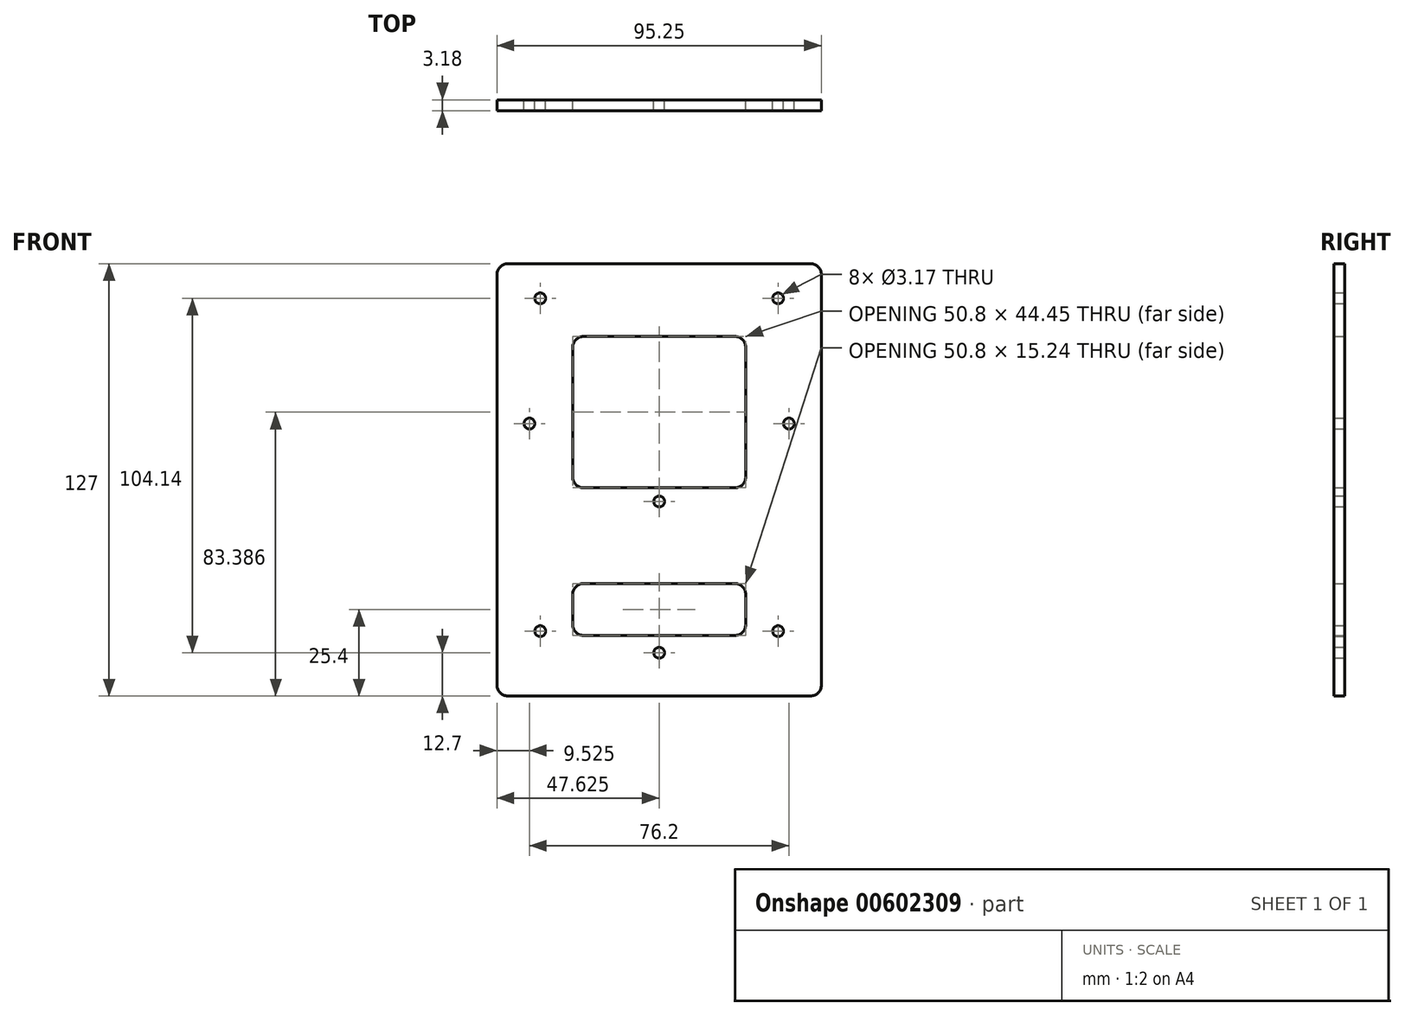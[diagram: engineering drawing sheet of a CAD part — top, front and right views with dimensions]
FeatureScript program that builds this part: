
annotation { "Feature Type Name" : "Feature", "Feature Type Description" : "" }
export const myFeature = defineFeature(function(context is Context, id is Id, definition is map)
    precondition{}
    {
        {
            var Q0;
            Q0=qCreatedBy(makeId("Front.planeOp"),FACE);
            var sketch = newSketch(context, id + "F0", { "sketchPlane" : qUnion([Q0])});
            skLineSegment(sketch, "E0.bottom", {"start": v(3.17, 0) * mm, "end": v(92.08, 0) * mm});
            skLineSegment(sketch, "E1.MirrorCS", {"start": v(0, -3.17) * mm, "end": v(0, -123.83) * mm});
            skLineSegment(sketch, "E2.MirrorCS", {"start": v(95.25, -3.17) * mm, "end": v(95.25, -123.83) * mm});
            skCircle(sketch, "E3.MirrorC", {"center": v(85.73, -46.95) * mm, "radius": 31.75 * mm, "construction": true});
            skCircle(sketch, "E4.MirrorC", {"center": v(47.63, -69.85) * mm, "radius": 31.75 * mm, "construction": true});
            skCircle(sketch, "E5.MirrorC", {"center": v(85.73, -46.95) * mm, "radius": 1.59 * mm});
            skLineSegment(sketch, "E6.MirrorCS", {"start": v(47.63, -127) * mm, "end": v(47.62, 0) * mm, "construction": true});
            skLineSegment(sketch, "E7.MirrorCS", {"start": v(3.17, -127) * mm, "end": v(92.08, -127) * mm});
            skCircle(sketch, "E8.MirrorC", {"center": v(9.52, -46.95) * mm, "radius": 1.59 * mm});
            skCircle(sketch, "E9.MirrorC", {"center": v(9.52, -46.95) * mm, "radius": 31.75 * mm, "construction": true});
            skCircle(sketch, "E10.MirrorC", {"center": v(47.63, -69.85) * mm, "radius": 1.59 * mm});
            skCircle(sketch, "E11.MirrorC", {"center": v(47.63, -69.85) * mm, "radius": 12.7 * mm, "construction": true});
            skCircle(sketch, "E12.MirrorC", {"center": v(47.62, -114.3) * mm, "radius": 12.7 * mm, "construction": true});
            skCircle(sketch, "E13.MirrorC", {"center": v(47.62, -114.3) * mm, "radius": 1.59 * mm});
            skCircle(sketch, "E14", {"center": v(12.7, -10.16) * mm, "radius": 1.59 * mm});
            skCircle(sketch, "E15", {"center": v(12.7, -107.95) * mm, "radius": 1.59 * mm});
            skCircle(sketch, "E16.MirrorC", {"center": v(82.55, -10.16) * mm, "radius": 1.59 * mm});
            skCircle(sketch, "E17.MirrorC", {"center": v(82.55, -107.95) * mm, "radius": 1.59 * mm});
            skLineSegment(sketch, "E18.bottom", {"start": v(25.4, -21.39) * mm, "end": v(69.85, -21.39) * mm});
            skLineSegment(sketch, "E18.top", {"start": v(25.4, -65.84) * mm, "end": v(69.85, -65.84) * mm});
            skLineSegment(sketch, "E18.left", {"start": v(22.23, -24.56) * mm, "end": v(22.23, -62.66) * mm});
            skLineSegment(sketch, "E18.right", {"start": v(73.03, -24.56) * mm, "end": v(73.03, -62.66) * mm});
            skPoint(sketch, "E18.middle", {"position": v(47.63, -43.61) * mm});
            skLineSegment(sketch, "E19.bottom", {"start": v(69.85, -93.98) * mm, "end": v(25.4, -93.98) * mm});
            skLineSegment(sketch, "E19.top", {"start": v(69.85, -109.22) * mm, "end": v(25.4, -109.22) * mm});
            skLineSegment(sketch, "E19.left", {"start": v(73.03, -97.15) * mm, "end": v(73.03, -106.05) * mm});
            skLineSegment(sketch, "E19.right", {"start": v(22.23, -97.15) * mm, "end": v(22.23, -106.05) * mm});
            skPoint(sketch, "E19.middle", {"position": v(47.63, -101.6) * mm});
            skPoint(sketch, "E20.visualSharp", {"position": v(22.23, -21.39) * mm});
            skArc(sketch, "E20.filletArc", {"start": v(25.4, -21.39) * mm, "mid": v(23.15, -22.32) * mm, "end": v(22.23, -24.56) * mm});
            skPoint(sketch, "E21.visualSharp", {"position": v(73.03, -21.39) * mm});
            skArc(sketch, "E21.filletArc", {"start": v(73.03, -24.56) * mm, "mid": v(72.1, -22.32) * mm, "end": v(69.85, -21.39) * mm});
            skPoint(sketch, "E22.visualSharp", {"position": v(73.03, -65.84) * mm});
            skArc(sketch, "E22.filletArc", {"start": v(69.85, -65.84) * mm, "mid": v(72.1, -64.9) * mm, "end": v(73.03, -62.66) * mm});
            skPoint(sketch, "E23.visualSharp", {"position": v(22.23, -65.84) * mm});
            skArc(sketch, "E23.filletArc", {"start": v(22.23, -62.66) * mm, "mid": v(23.15, -64.9) * mm, "end": v(25.4, -65.84) * mm});
            skPoint(sketch, "E24.visualSharp", {"position": v(22.23, -93.98) * mm});
            skArc(sketch, "E24.filletArc", {"start": v(25.4, -93.98) * mm, "mid": v(23.15, -94.9) * mm, "end": v(22.23, -97.15) * mm});
            skPoint(sketch, "E25.visualSharp", {"position": v(73.03, -93.98) * mm});
            skArc(sketch, "E25.filletArc", {"start": v(73.02, -97.15) * mm, "mid": v(72.1, -94.9) * mm, "end": v(69.85, -93.98) * mm});
            skPoint(sketch, "E26.visualSharp", {"position": v(73.03, -109.22) * mm});
            skArc(sketch, "E26.filletArc", {"start": v(69.85, -109.22) * mm, "mid": v(72.1, -108.3) * mm, "end": v(73.02, -106.05) * mm});
            skPoint(sketch, "E27.visualSharp", {"position": v(22.23, -109.22) * mm});
            skArc(sketch, "E27.filletArc", {"start": v(22.23, -106.05) * mm, "mid": v(23.15, -108.3) * mm, "end": v(25.4, -109.22) * mm});
            skPoint(sketch, "E28.visualSharp", {"position": v(95.25, 0) * mm});
            skArc(sketch, "E28.filletArc", {"start": v(95.25, -3.17) * mm, "mid": v(94.32, -0.93) * mm, "end": v(92.08, 0) * mm});
            skPoint(sketch, "E29.visualSharp", {"position": v(0, 0) * mm});
            skArc(sketch, "E29.filletArc", {"start": v(3.17, 0) * mm, "mid": v(0.93, -0.93) * mm, "end": v(0, -3.17) * mm});
            skPoint(sketch, "E30.visualSharp", {"position": v(0, -127) * mm});
            skArc(sketch, "E30.filletArc", {"start": v(0, -123.83) * mm, "mid": v(0.93, -126.07) * mm, "end": v(3.17, -127) * mm});
            skPoint(sketch, "E31.visualSharp", {"position": v(95.25, -127) * mm});
            skArc(sketch, "E31.filletArc", {"start": v(92.08, -127) * mm, "mid": v(94.32, -126.07) * mm, "end": v(95.25, -123.83) * mm});
            skSolve(sketch);
        }
        {
            var Q0;
            Q0=qSketchRegion(id+"F0",true);
            extrude(context, id + "F1", {"entities" : qUnion([Q0]), "depth" : 3.17 * mm, "offsetDistance" : 25.4 * mm});
        }
    });
